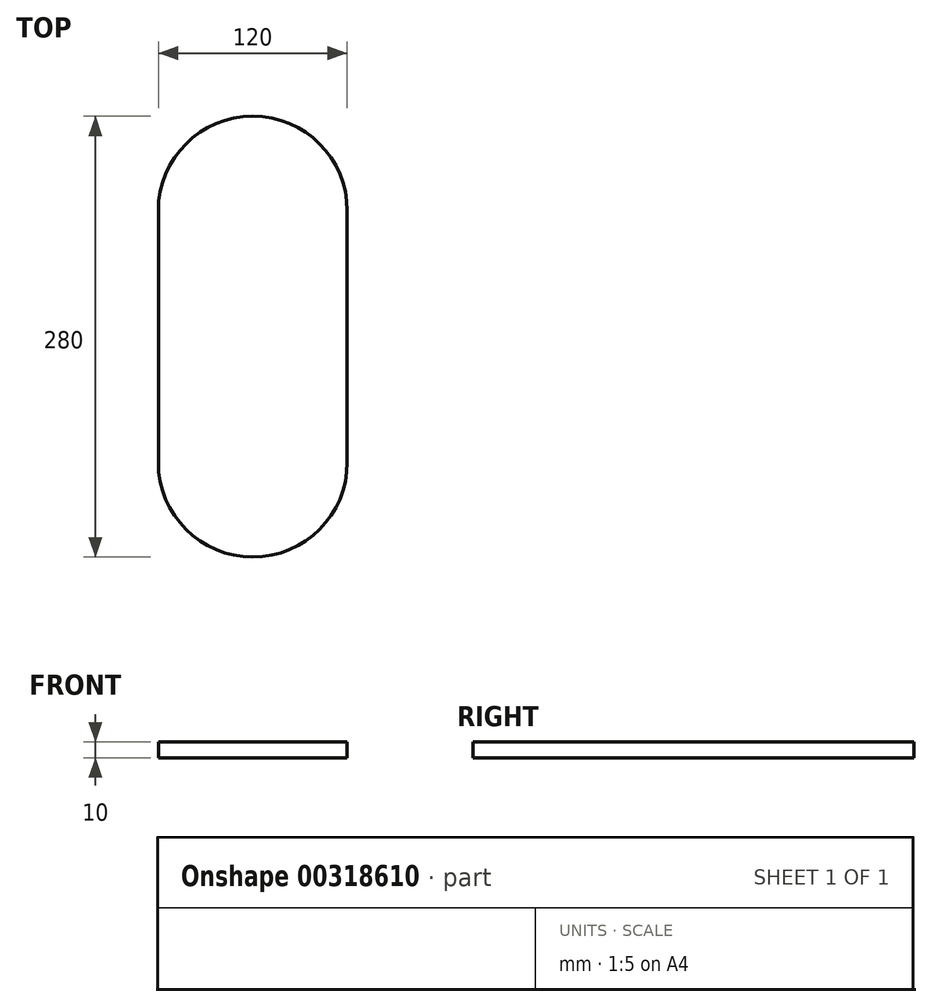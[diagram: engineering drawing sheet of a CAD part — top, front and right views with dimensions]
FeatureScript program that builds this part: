
annotation { "Feature Type Name" : "Feature", "Feature Type Description" : "" }
export const myFeature = defineFeature(function(context is Context, id is Id, definition is map)
    precondition{}
    {
        {
            var Q0;
            Q0=qCreatedBy(makeId("Top.planeOp"),FACE);
            var sketch = newSketch(context, id + "F0", { "sketchPlane" : qUnion([Q0])});
            skLineSegment(sketch, "E0.left", {"start": v(60, 80) * mm, "end": v(60, -80) * mm});
            skLineSegment(sketch, "E0.right", {"start": v(-60, 80) * mm, "end": v(-60, -80) * mm});
            skPoint(sketch, "E0.middle", {"position": v(0, 0) * mm});
            skArc(sketch, "E1", {"start": v(-60, 80) * mm, "mid": v(0, 140) * mm, "end": v(60, 80) * mm});
            skArc(sketch, "E2", {"start": v(-60, -80) * mm, "mid": v(0, -140) * mm, "end": v(60, -80) * mm});
            skSolve(sketch);
        }
        {
            var Q0;
            Q0 = qSketchRegion(id + "F0", true);
            extrude(context, id + "F1", {"entities" : qUnion([Q0]), "depth" : 10 * mm});
        }
    });
